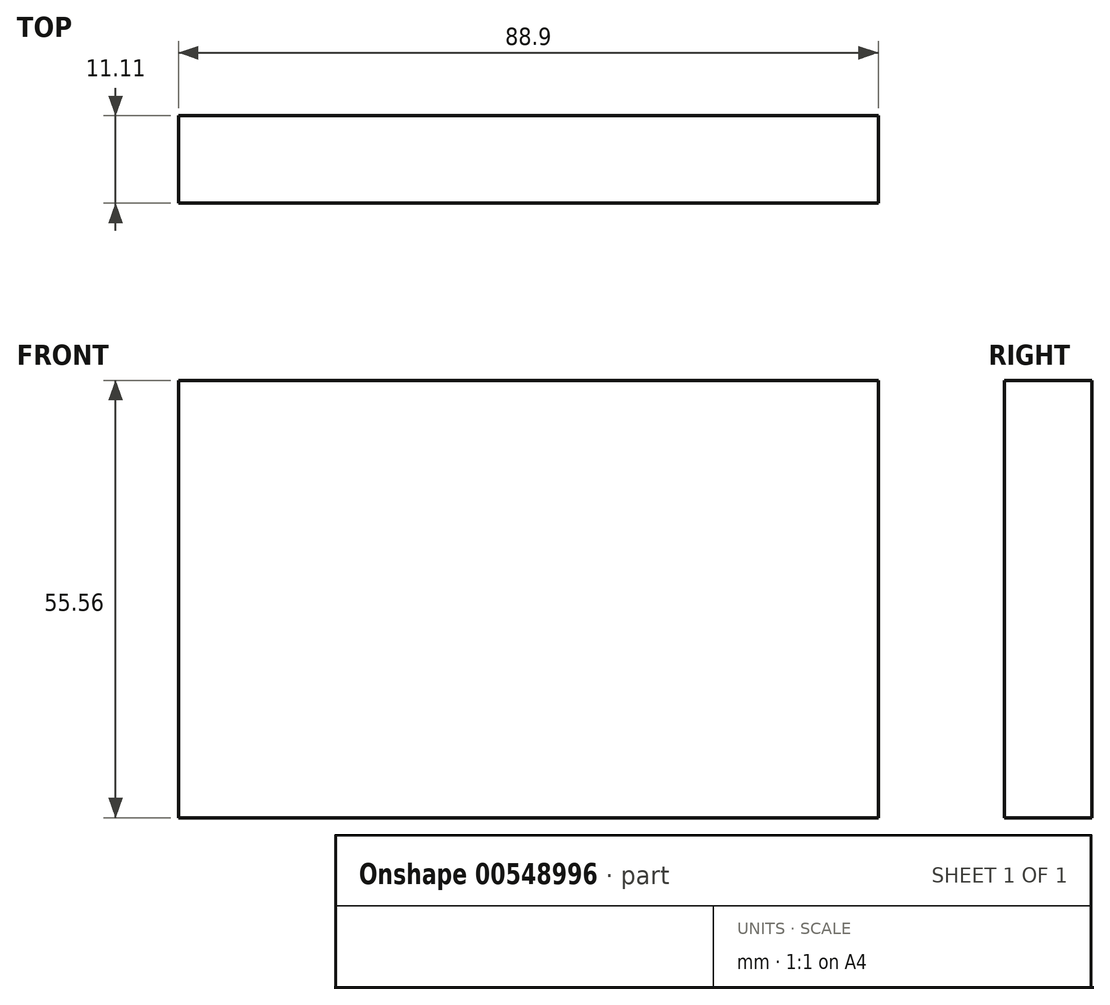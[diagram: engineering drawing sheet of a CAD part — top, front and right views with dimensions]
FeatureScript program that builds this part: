
annotation { "Feature Type Name" : "Feature", "Feature Type Description" : "" }
export const myFeature = defineFeature(function(context is Context, id is Id, definition is map)
    precondition{}
    {
        {
            var Q0;
            Q0=qCreatedBy(makeId("Front.planeOp"),FACE);
            var sketch = newSketch(context, id + "F0", { "sketchPlane" : qUnion([Q0])});
            skLineSegment(sketch, "E0.bottom", {"start": v(44.45, -27.78) * mm, "end": v(-44.45, -27.78) * mm});
            skLineSegment(sketch, "E0.top", {"start": v(44.45, 27.78) * mm, "end": v(-44.45, 27.78) * mm});
            skLineSegment(sketch, "E0.left", {"start": v(44.45, -27.78) * mm, "end": v(44.45, 27.78) * mm});
            skLineSegment(sketch, "E0.right", {"start": v(-44.45, -27.78) * mm, "end": v(-44.45, 27.78) * mm});
            skPoint(sketch, "E0.middle", {"position": v(0, 0) * mm});
            skSolve(sketch);
        }
        {
            var Q0;
            Q0 = qSketchRegion(id + "F0", true);
            extrude(context, id + "F1", {"entities" : qUnion([Q0]), "depth" : 11.1 * mm, "offsetDistance" : 25.4 * mm});
        }
    });
